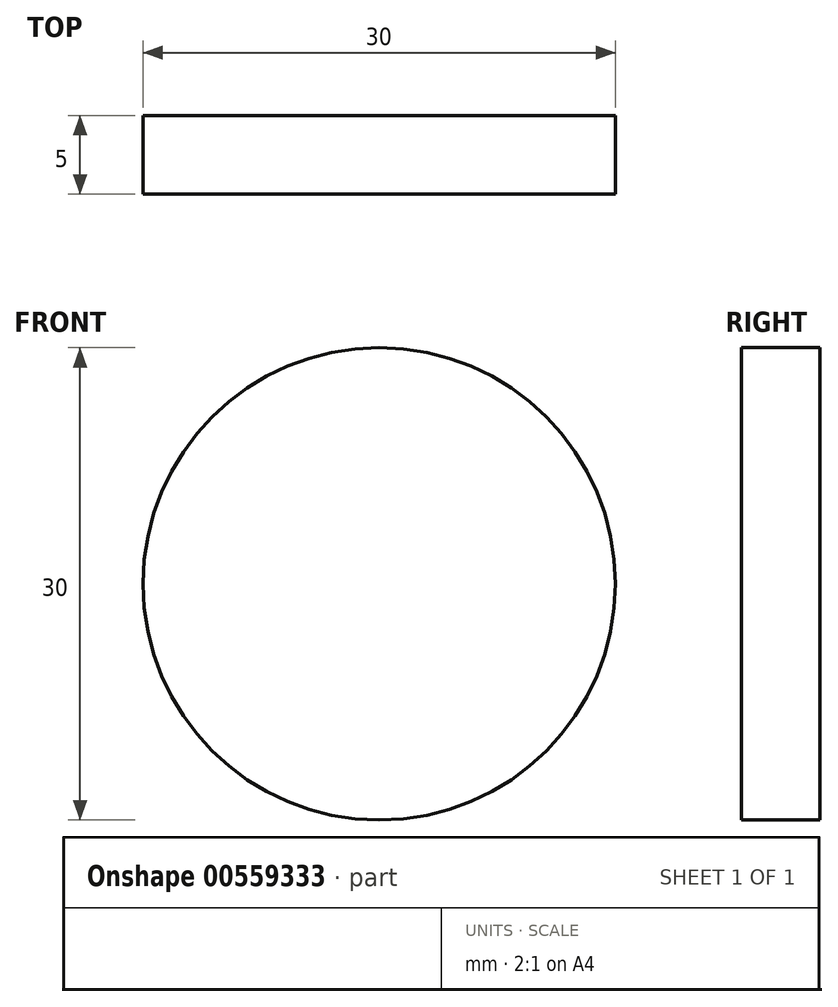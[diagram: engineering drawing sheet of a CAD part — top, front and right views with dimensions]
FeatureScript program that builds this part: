
annotation { "Feature Type Name" : "Feature", "Feature Type Description" : "" }
export const myFeature = defineFeature(function(context is Context, id is Id, definition is map)
    precondition{}
    {
        {
            var Q0;
            Q0=qCreatedBy(makeId("Front.planeOp"),FACE);
            var sketch = newSketch(context, id + "F0", { "sketchPlane" : qUnion([Q0])});
            skCircle(sketch, "E0", {"center": v(0, 0) * mm, "radius": 15 * mm});
            skSolve(sketch);
        }
        {
            var Q0;
            Q0=sQuery(id+"F0.wireOp",EDGE,"E0");
            extrude(context, id + "F1", {"bodyType" : ToolBodyType.SURFACE, "surfaceEntities" : qUnion([Q0]), "depth" : 5 * mm, "offsetDistance" : 25 * mm});
        }
    });
